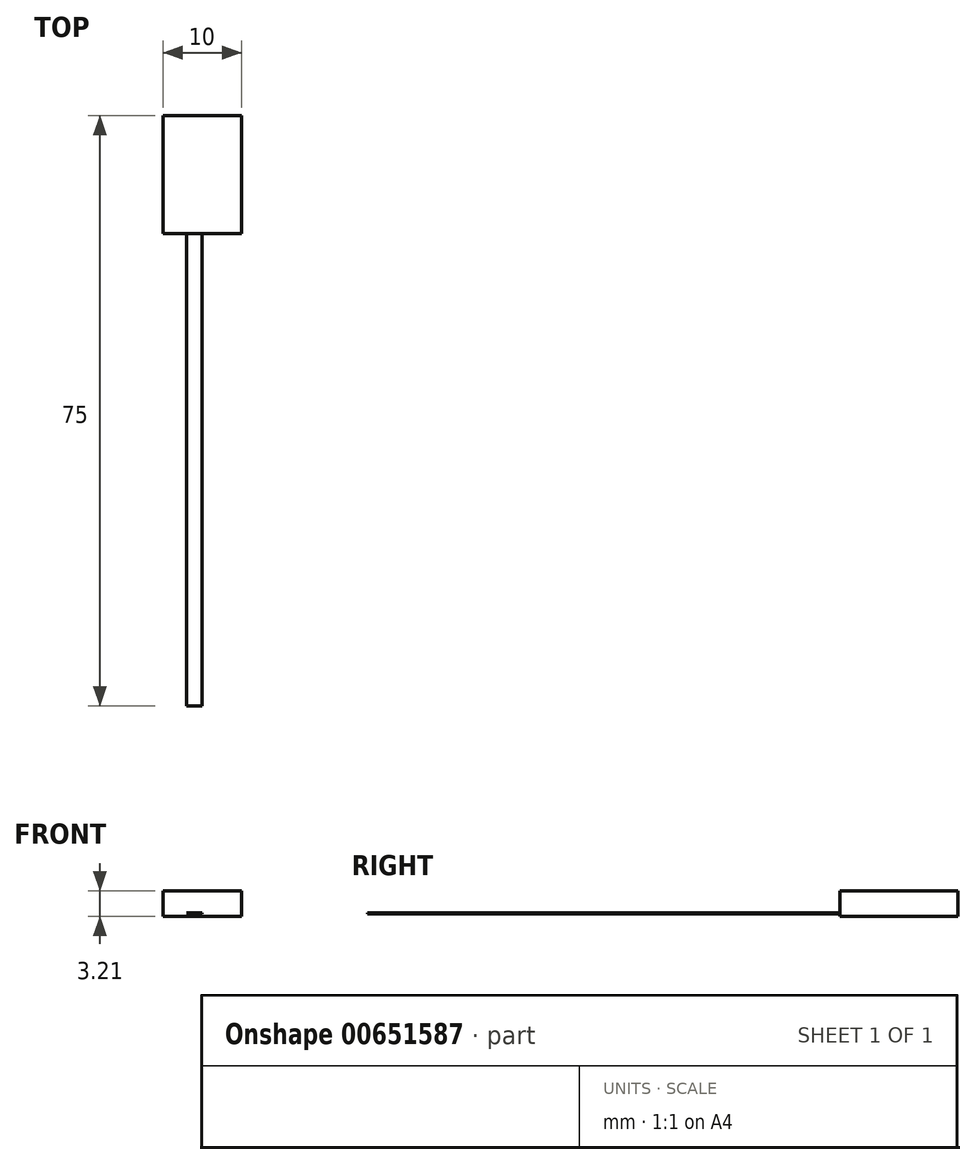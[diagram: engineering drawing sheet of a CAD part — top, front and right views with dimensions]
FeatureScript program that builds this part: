
annotation { "Feature Type Name" : "Feature", "Feature Type Description" : "" }
export const myFeature = defineFeature(function(context is Context, id is Id, definition is map)
    precondition{}
    {
        {
            var Q0;
            Q0=qCreatedBy(makeId("Front.planeOp"),FACE);
            var sketch = newSketch(context, id + "F0", { "sketchPlane" : qUnion([Q0])});
            skCircle(sketch, "E0", {"center": v(0, 0) * mm, "radius": 1.4 * mm});
            skEllipse(sketch, "E1", {"center": v(0, 1.32) * mm, "majorRadius": 4.3 * mm, "minorRadius": 1.32 * mm, "majorAxis": v(-1, 0)});
            skLineSegment(sketch, "E2", {"start": v(-1.99, 0.15) * mm, "end": v(1.99, 0.15) * mm});
            skLineSegment(sketch, "E3", {"start": v(0, 0) * mm, "end": v(0, 0.15) * mm});
            skSolve(sketch);
        }
        {
            var Q0;
            {var subQ0=sQuery(id+"F0.wireOp",EDGE,"E2");var subQ1=sQuery(id+"F0.wireOp",EDGE,"E0");var subQ2=makeQuery(id+"F0.imprint","INTERSECT",VERTEX,{"disambiguationData":[OD(0.0)],"derivedFrom":[subQ1,subQ0]});Q0=makeQuery(id+"F0.imprint","IMPRINT",FACE,{"disambiguationData":[TD([[makeQuery(id+"F0.imprint","IMPRINT",EDGE,{"disambiguationData":[TD([[subQ2,-1.0]])],"derivedFrom":subQ1}),-1.0]])]});}
            var Q1;
            {var subQ0=sQuery(id+"F0.wireOp",EDGE,"E2");var subQ1=sQuery(id+"F0.wireOp",EDGE,"E0");var subQ2=makeQuery(id+"F0.imprint","INTERSECT",VERTEX,{"disambiguationData":[OD(0.0)],"derivedFrom":[subQ1,subQ0]});Q1=makeQuery(id+"F0.imprint","IMPRINT",FACE,{"disambiguationData":[TD([[makeQuery(id+"F0.imprint","IMPRINT",EDGE,{"disambiguationData":[TD([[subQ2,-1.0]])],"derivedFrom":subQ1}),1.0]])]});}
            extrude(context, id + "F1", {"entities" : qUnion([Q0, Q1]), "oppositeDirection" : true, "depth" : 60 * mm});
        }
        {
            var Q0;
            Q0=makeQuery(id+"F1.opExtrude","CAP_FACE",FACE,{"disambiguationData":[OSD([sQuery(id+"F0.wireOp",EDGE,"E1")])],"isStart":false});
            var sketch = newSketch(context, id + "F2", { "sketchPlane" : qUnion([Q0])});
            skPoint(sketch, "E4", {"position": v(0, 1.32) * mm});
            skLineSegment(sketch, "E5.bottom", {"start": v(-5, 2.93) * mm, "end": v(5, 2.93) * mm});
            skLineSegment(sketch, "E5.top", {"start": v(-5, -0.28) * mm, "end": v(5, -0.28) * mm});
            skLineSegment(sketch, "E5.left", {"start": v(-5, 2.93) * mm, "end": v(-5, -0.28) * mm});
            skLineSegment(sketch, "E5.right", {"start": v(5, 2.93) * mm, "end": v(5, -0.28) * mm});
            skSolve(sketch);
        }
        {
            var Q0;
            Q0=makeQuery(id+"F2.imprint","IMPRINT",FACE,{"disambiguationData":[TD([[makeQuery(id+"F2.imprint","IMPRINT",EDGE,{"derivedFrom":sQuery(id+"F2.wireOp",EDGE,"E5.bottom")}),-1.0]])]});
            var Q1;
            Q1=makeQuery(id+"F2.imprint","IMPRINT",FACE,{"disambiguationData":[TD([[makeQuery(id+"F2.imprint","IMPRINT",EDGE,{"derivedFrom":makeQuery(id+"F1.opExtrude","CAP_EDGE",EDGE,{"disambiguationData":[OSD([sQuery(id+"F0.wireOp",EDGE,"E1")])],"isStart":false})}),-1.0]])]});
            extrude(context, id + "F3", {"entities" : qUnion([Q0, Q1]), "operationType" : NewBodyOperationType.ADD, "depth" : 15 * mm});
        }
    });
